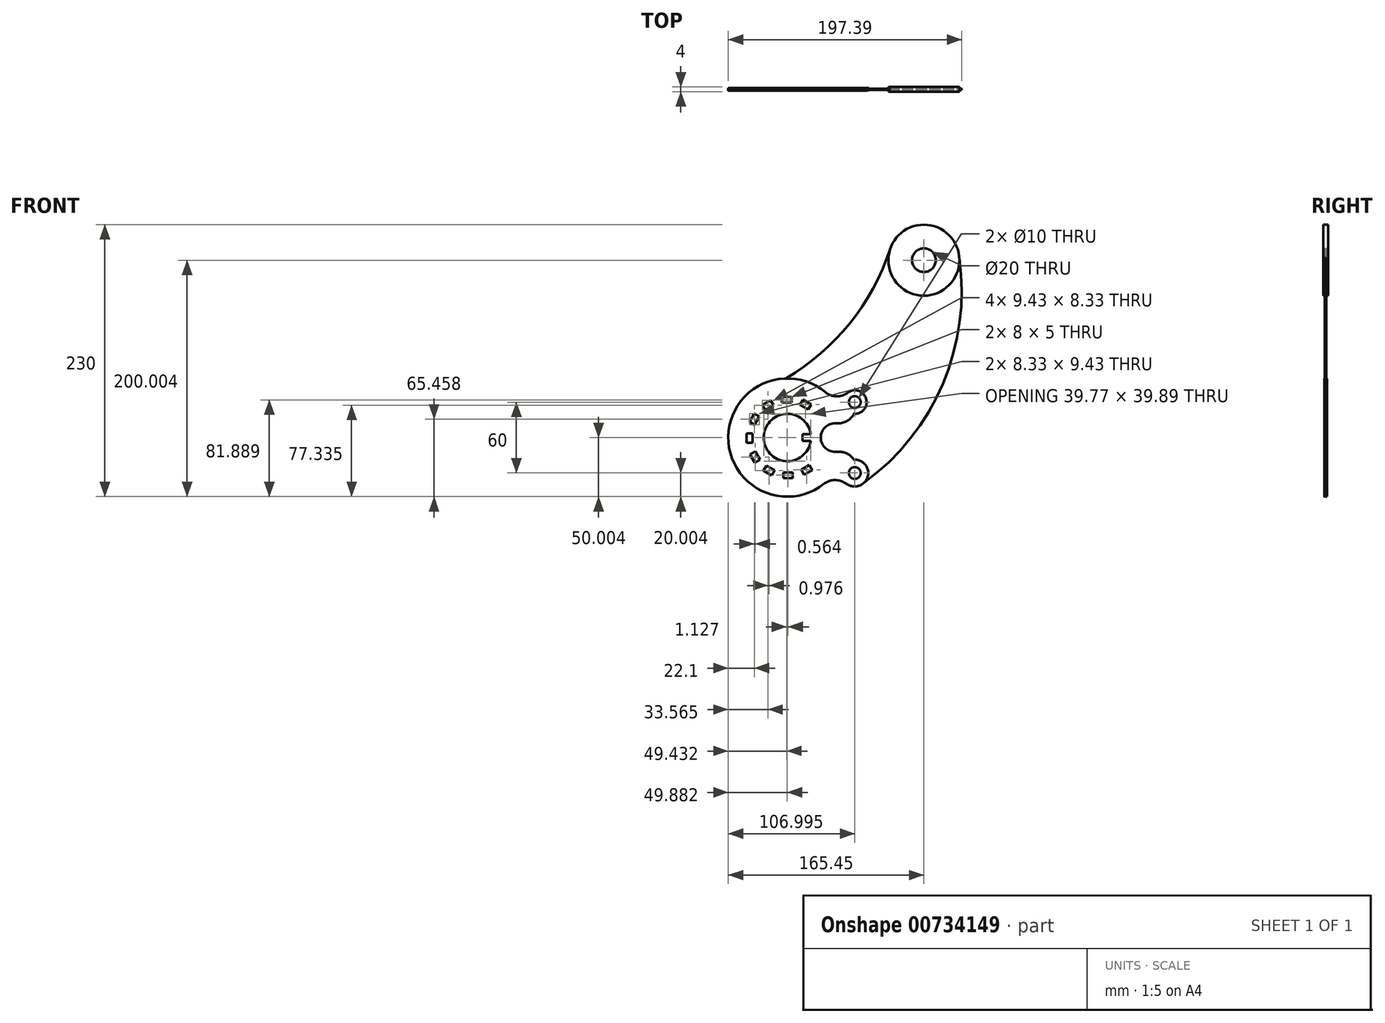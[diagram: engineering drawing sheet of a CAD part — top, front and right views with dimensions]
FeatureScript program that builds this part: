
annotation { "Feature Type Name" : "Feature", "Feature Type Description" : "" }
export const myFeature = defineFeature(function(context is Context, id is Id, definition is map)
    precondition{}
    {
        {
            var Q0;
            Q0=qCreatedBy(makeId("Front.planeOp"),FACE);
            var sketch = newSketch(context, id + "F0", { "sketchPlane" : qUnion([Q0])});
            skCircle(sketch, "E0", {"center": v(75.2, 116.81) * mm, "radius": 10 * mm});
            skCircle(sketch, "E1", {"center": v(75.2, 116.81) * mm, "radius": 30 * mm});
            skLineSegment(sketch, "E2", {"start": v(-20.48, -30.19) * mm, "end": v(-27.48, -30.19) * mm});
            skLineSegment(sketch, "E3", {"start": v(-27.48, -30.19) * mm, "end": v(-27.48, -36.19) * mm});
            skLineSegment(sketch, "E4", {"start": v(-27.48, -36.19) * mm, "end": v(-20.48, -36.19) * mm});
            skArc(sketch, "E5", {"start": v(-20.48, -30.19) * mm, "mid": v(-60.25, -33.19) * mm, "end": v(-20.48, -36.19) * mm});
            skCircle(sketch, "E6", {"center": v(16.75, -3.19) * mm, "radius": 5 * mm});
            skCircle(sketch, "E7", {"center": v(16.75, -63.19) * mm, "radius": 5 * mm});
            skArc(sketch, "E8", {"start": v(-8.13, 5.13) * mm, "mid": v(-23.95, 14.08) * mm, "end": v(-41.91, 16.79) * mm});
            skArc(sketch, "E9", {"start": v(16.02, -13.16) * mm, "mid": v(26.32, -0.3) * mm, "end": v(10.65, 4.74) * mm});
            skArc(sketch, "E10", {"start": v(0, -21.19) * mm, "mid": v(-12, -33.19) * mm, "end": v(0, -45.19) * mm});
            skArc(sketch, "E11", {"start": v(16.02, -51.83) * mm, "mid": v(10.62, -46.95) * mm, "end": v(3.56, -45.19) * mm});
            skArc(sketch, "E12", {"start": v(11.32, -73.19) * mm, "mid": v(27.85, -65.63) * mm, "end": v(16.02, -51.83) * mm});
            skArc(sketch, "E13", {"start": v(-41.65, 16.8) * mm, "mid": v(12.28, 63.24) * mm, "end": v(46.53, 125.63) * mm});
            skArc(sketch, "E14", {"start": v(22.3, -73.11) * mm, "mid": v(90.72, 11.04) * mm, "end": v(105.15, 118.53) * mm});
            skArc(sketch, "E15", {"start": v(-8.13, 5.13) * mm, "mid": v(0.77, 1.65) * mm, "end": v(9.97, 4.25) * mm});
            skLineSegment(sketch, "E16.bottom", {"start": v(-44.82, 1.2) * mm, "end": v(-36.82, 1.2) * mm});
            skLineSegment(sketch, "E16.top", {"start": v(-44.82, -3.8) * mm, "end": v(-36.82, -3.8) * mm});
            skLineSegment(sketch, "E16.left", {"start": v(-44.82, 1.2) * mm, "end": v(-44.82, -3.8) * mm});
            skLineSegment(sketch, "E16.right", {"start": v(-36.82, 1.2) * mm, "end": v(-36.82, -3.8) * mm});
            skArc(sketch, "E17", {"start": v(-41.91, 16.79) * mm, "mid": v(-87.2, -50.4) * mm, "end": v(-9.23, -72.4) * mm});
            skLineSegment(sketch, "E18.2.0", {"start": v(23.45, 38.21) * mm, "end": v(19.12, 40.71) * mm});
            skPoint(sketch, "E18.center", {"position": v(0, 0) * mm});
            skLineSegment(sketch, "E19.1.0", {"start": v(-61.4, -5.69) * mm, "end": v(-58.9, -10.02) * mm});
            skLineSegment(sketch, "E19.1.1", {"start": v(-61.4, -5.69) * mm, "end": v(-54.47, -1.69) * mm});
            skLineSegment(sketch, "E19.1.2", {"start": v(-58.9, -10.02) * mm, "end": v(-51.97, -6.02) * mm});
            skLineSegment(sketch, "E19.1.3", {"start": v(-54.47, -1.69) * mm, "end": v(-51.97, -6.02) * mm});
            skLineSegment(sketch, "E19.2.0", {"start": v(-72.31, -19.95) * mm, "end": v(-67.98, -22.45) * mm});
            skLineSegment(sketch, "E19.2.1", {"start": v(-72.31, -19.95) * mm, "end": v(-68.31, -13.02) * mm});
            skLineSegment(sketch, "E19.2.2", {"start": v(-67.98, -22.45) * mm, "end": v(-63.98, -15.52) * mm});
            skLineSegment(sketch, "E19.2.3", {"start": v(-68.31, -13.02) * mm, "end": v(-63.98, -15.52) * mm});
            skLineSegment(sketch, "E19.3.0", {"start": v(-74.64, -37.75) * mm, "end": v(-69.64, -37.75) * mm});
            skLineSegment(sketch, "E19.3.1", {"start": v(-74.64, -37.75) * mm, "end": v(-74.64, -29.75) * mm});
            skLineSegment(sketch, "E19.3.2", {"start": v(-69.64, -37.75) * mm, "end": v(-69.64, -29.75) * mm});
            skLineSegment(sketch, "E19.3.3", {"start": v(-74.64, -29.75) * mm, "end": v(-69.64, -29.75) * mm});
            skLineSegment(sketch, "E19.4.0", {"start": v(-67.75, -54.33) * mm, "end": v(-63.42, -51.83) * mm});
            skLineSegment(sketch, "E19.4.1", {"start": v(-67.75, -54.33) * mm, "end": v(-71.75, -47.4) * mm});
            skLineSegment(sketch, "E19.4.2", {"start": v(-63.42, -51.83) * mm, "end": v(-67.42, -44.9) * mm});
            skLineSegment(sketch, "E19.4.3", {"start": v(-71.75, -47.4) * mm, "end": v(-67.42, -44.9) * mm});
            skLineSegment(sketch, "E19.5.0", {"start": v(-53.5, -65.25) * mm, "end": v(-51, -60.92) * mm});
            skLineSegment(sketch, "E19.5.1", {"start": v(-53.5, -65.25) * mm, "end": v(-60.42, -61.25) * mm});
            skLineSegment(sketch, "E19.5.2", {"start": v(-51, -60.92) * mm, "end": v(-57.92, -56.92) * mm});
            skLineSegment(sketch, "E19.5.3", {"start": v(-60.42, -61.25) * mm, "end": v(-57.92, -56.92) * mm});
            skLineSegment(sketch, "E19.6.0", {"start": v(-35.7, -67.57) * mm, "end": v(-35.7, -62.57) * mm});
            skLineSegment(sketch, "E19.6.1", {"start": v(-35.7, -67.57) * mm, "end": v(-43.7, -67.57) * mm});
            skLineSegment(sketch, "E19.6.2", {"start": v(-35.7, -62.57) * mm, "end": v(-43.7, -62.57) * mm});
            skLineSegment(sketch, "E19.6.3", {"start": v(-43.7, -67.57) * mm, "end": v(-43.7, -62.57) * mm});
            skLineSegment(sketch, "E19.7.0", {"start": v(-19.1, -60.68) * mm, "end": v(-21.6, -56.35) * mm});
            skLineSegment(sketch, "E19.7.1", {"start": v(-19.1, -60.68) * mm, "end": v(-26.04, -64.68) * mm});
            skLineSegment(sketch, "E19.7.2", {"start": v(-21.6, -56.35) * mm, "end": v(-28.54, -60.35) * mm});
            skLineSegment(sketch, "E19.7.3", {"start": v(-26.04, -64.68) * mm, "end": v(-28.54, -60.35) * mm});
            skLineSegment(sketch, "E19.11.0", {"start": v(-27.01, -1.13) * mm, "end": v(-29.51, -5.46) * mm});
            skLineSegment(sketch, "E19.11.1", {"start": v(-27.01, -1.13) * mm, "end": v(-20.09, -5.13) * mm});
            skLineSegment(sketch, "E19.11.2", {"start": v(-29.51, -5.46) * mm, "end": v(-22.59, -9.46) * mm});
            skLineSegment(sketch, "E19.11.3", {"start": v(-20.09, -5.13) * mm, "end": v(-22.59, -9.46) * mm});
            skLineSegment(sketch, "E20", {"start": v(0, -45.19) * mm, "end": v(3.56, -45.19) * mm});
            skArc(sketch, "E21", {"start": v(7.23, -70.97) * mm, "mid": v(-1.21, -69.21) * mm, "end": v(-9.23, -72.4) * mm});
            skLineSegment(sketch, "E22", {"start": v(7.23, -70.97) * mm, "end": v(11.32, -73.19) * mm});
            skArc(sketch, "E23", {"start": v(2.74, -21.19) * mm, "mid": v(10.5, -19.02) * mm, "end": v(16.02, -13.16) * mm});
            skLineSegment(sketch, "E24", {"start": v(0, -21.19) * mm, "end": v(2.74, -21.19) * mm});
            skArc(sketch, "E25", {"start": v(9.97, 4.25) * mm, "mid": v(10.31, 4.49) * mm, "end": v(10.65, 4.74) * mm});
            skSolve(sketch);
        }
        {
            var Q0;
            Q0=makeQuery(id+"F0.imprint","IMPRINT",FACE,{"disambiguationData":[TD([[makeQuery(id+"F0.imprint","IMPRINT",EDGE,{"derivedFrom":sQuery(id+"F0.wireOp",EDGE,"E2")}),1.0]])]});
            extrude(context, id + "F1", {"entities" : qUnion([Q0]), "endBound" : BoundingType.SYMMETRIC, "depth" : 2.3 * mm, "offsetDistance" : 25 * mm});
        }
        {
            var Q0;
            Q0=makeQuery(id+"F0.imprint","IMPRINT",FACE,{"disambiguationData":[TD([[makeQuery(id+"F0.imprint","IMPRINT",EDGE,{"derivedFrom":sQuery(id+"F0.wireOp",EDGE,"E0")}),-1.0]])]});
            extrude(context, id + "F2", {"entities" : qUnion([Q0]), "endBound" : BoundingType.SYMMETRIC, "depth" : 4 * mm, "offsetDistance" : 25 * mm});
        }
        {
            var Q0;
            Q0=makeQuery(id+"F0.imprint","IMPRINT",FACE,{"disambiguationData":[TD([[makeQuery(id+"F0.imprint","IMPRINT",EDGE,{"derivedFrom":sQuery(id+"F0.wireOp",EDGE,"E9")}),-1.0]])]});
            extrude(context, id + "F3", {"entities" : qUnion([Q0]), "endBound" : BoundingType.SYMMETRIC, "depth" : 1.2 * mm, "offsetDistance" : 25 * mm});
        }
        {
            var Q0;
            {var subQ0=sQuery(id+"F0.wireOp",EDGE,"E12");Q0=makeQuery(id+"F1.opExtrude","CAP_EDGE",EDGE,{"disambiguationData":[OSD([subQ0]),TDD([makeQuery(id+"F0.imprint","IMPRINT",EDGE,{"disambiguationData":[TD([[makeQuery(id+"F0.imprint","INTERSECT",VERTEX,{"derivedFrom":[sQuery(id+"F0.wireOp",EDGE,"E11"),subQ0]}),1.0]])],"derivedFrom":subQ0})])],"isStart":false});}
            var Q1;
            Q1=makeQuery(id+"F1.opExtrude","CAP_EDGE",EDGE,{"disambiguationData":[OSD([sQuery(id+"F0.wireOp",EDGE,"E11")])],"isStart":false});
            var Q2;
            Q2=makeQuery(id+"F1.opExtrude","CAP_EDGE",EDGE,{"disambiguationData":[OSD([sQuery(id+"F0.wireOp",EDGE,"E10")])],"isStart":false});
            var Q3;
            Q3=makeQuery(id+"F1.opExtrude","CAP_EDGE",EDGE,{"disambiguationData":[OSD([sQuery(id+"F0.wireOp",EDGE,"ypfHy1js-oe6y-aGFT-zmz0-TJu4ysli4Agj")])],"isStart":false});
            var Q4;
            Q4=makeQuery(id+"F1.opExtrude","CAP_EDGE",EDGE,{"disambiguationData":[OSD([sQuery(id+"F0.wireOp",EDGE,"E9")])],"isStart":false});
            var Q5;
            Q5=makeQuery(id+"F3.opExtrude","CAP_EDGE",EDGE,{"disambiguationData":[OSD([sQuery(id+"F0.wireOp",EDGE,"E15")])],"isStart":false});
            var Q6;
            Q6=makeQuery(id+"F1.opExtrude","CAP_EDGE",EDGE,{"disambiguationData":[OSD([sQuery(id+"F0.wireOp",EDGE,"FNMor9hb-Umds-Lp7l-vPQD-XRPCCRxwyyA5")])],"isStart":false});
            var Q7;
            {var subQ0=sQuery(id+"F0.wireOp",EDGE,"E12");Q7=makeQuery(id+"F1.opExtrude","CAP_EDGE",EDGE,{"disambiguationData":[OSD([subQ0]),TDD([makeQuery(id+"F0.imprint","IMPRINT",EDGE,{"disambiguationData":[TD([[makeQuery(id+"F0.imprint","INTERSECT",VERTEX,{"derivedFrom":[sQuery(id+"F0.wireOp",EDGE,"FNMor9hb-Umds-Lp7l-vPQD-XRPCCRxwyyA5"),subQ0]}),-1.0]])],"derivedFrom":subQ0})])],"isStart":false});}
            var Q8;
            Q8=makeQuery(id+"F1.opExtrude","CAP_EDGE",EDGE,{"disambiguationData":[OSD([sQuery(id+"F0.wireOp",EDGE,"E14")])],"isStart":false});
            var Q9;
            Q9=makeQuery(id+"F3.opExtrude","CAP_EDGE",EDGE,{"disambiguationData":[OSD([sQuery(id+"F0.wireOp",EDGE,"E8")])],"isStart":false});
            fillet(context, id + "F4", {"entities" : qUnion([Q0, Q1, Q2, Q3, Q4, Q5, Q6, Q7, Q8, Q9]), "radius" : .25 * mm, "tangentPropagation" : true, "allowEdgeOverflow" : false});
        }
    });
